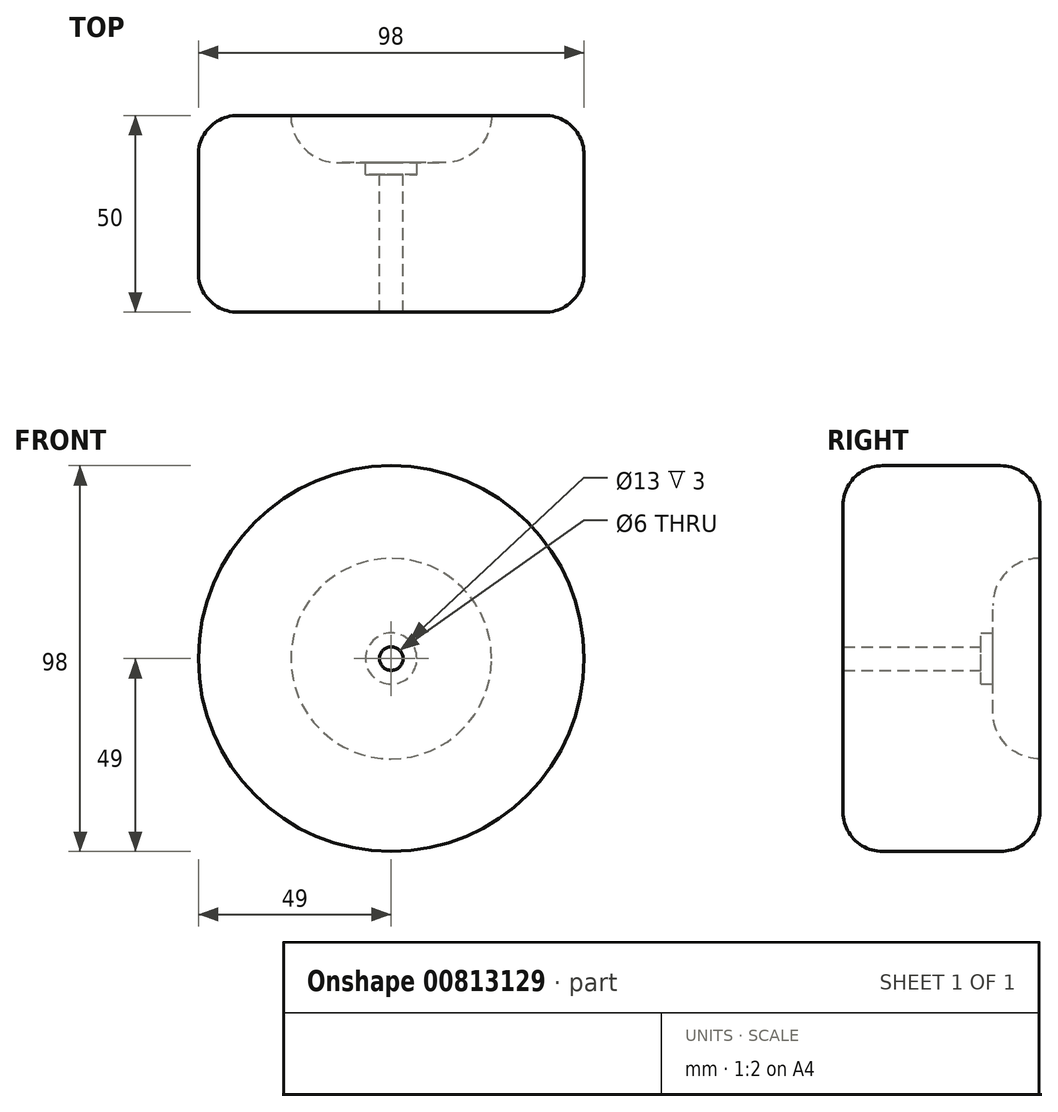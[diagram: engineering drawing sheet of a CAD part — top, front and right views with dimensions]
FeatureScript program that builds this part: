
annotation { "Feature Type Name" : "Feature", "Feature Type Description" : "" }
export const myFeature = defineFeature(function(context is Context, id is Id, definition is map)
    precondition{}
    {
        {
            var Q0;
            Q0=qCreatedBy(makeId("Front.planeOp"),FACE);
            var sketch = newSketch(context, id + "F0", { "sketchPlane" : qUnion([Q0])});
            skCircle(sketch, "E0", {"center": v(0, 0) * mm, "radius": 49 * mm});
            skSolve(sketch);
        }
        {
            var Q0;
            Q0=qSketchRegion(id+"F0",true);
            extrude(context, id + "F1", {"entities" : qUnion([Q0]), "depth" : 50 * mm, "offsetDistance" : 25 * mm});
        }
        {
            var Q0;
            Q0=makeQuery(id+"F1.opExtrude","CAP_EDGE",EDGE,{"disambiguationData":[OSD([sQuery(id+"F0.wireOp",EDGE,"E0")])],"isStart":false});
            var Q1;
            Q1=makeQuery(id+"F1.opExtrude","CAP_EDGE",EDGE,{"disambiguationData":[OSD([sQuery(id+"F0.wireOp",EDGE,"E0")])],"isStart":true});
            fillet(context, id + "F2", {"entities" : qUnion([Q0, Q1]), "radius" : 10 * mm, "tangentPropagation" : true, "allowEdgeOverflow" : false});
        }
        {
            var Q0;
            Q0=qCreatedBy(makeId("Front.planeOp"),FACE);
            var sketch = newSketch(context, id + "F3", { "sketchPlane" : qUnion([Q0])});
            skArc(sketch, "E1", {"start": v(-4.5, 48.8) * mm, "mid": v(0, 47.5) * mm, "end": v(4.5, 48.8) * mm});
            skArc(sketch, "E2.0", {"start": v(-4.5, 48.8) * mm, "mid": v(-9.56, 48.06) * mm, "end": v(-14.5, 46.8) * mm});
            skArc(sketch, "E3.1.0", {"start": v(-22.83, 43.35) * mm, "mid": v(-18.18, 43.9) * mm, "end": v(-14.5, 46.8) * mm});
            skArc(sketch, "E3.2.0", {"start": v(-37.69, 31.32) * mm, "mid": v(-33.6, 33.6) * mm, "end": v(-31.32, 37.69) * mm});
            skArc(sketch, "E3.3.0", {"start": v(-46.8, 14.5) * mm, "mid": v(-43.9, 18.18) * mm, "end": v(-43.35, 22.83) * mm});
            skArc(sketch, "E3.4.0", {"start": v(-48.8, -4.5) * mm, "mid": v(-47.5, 0) * mm, "end": v(-48.8, 4.5) * mm});
            skArc(sketch, "E3.5.0", {"start": v(-43.35, -22.83) * mm, "mid": v(-43.9, -18.18) * mm, "end": v(-46.8, -14.5) * mm});
            skArc(sketch, "E3.6.0", {"start": v(-31.32, -37.69) * mm, "mid": v(-33.6, -33.6) * mm, "end": v(-37.69, -31.32) * mm});
            skArc(sketch, "E3.7.0", {"start": v(-14.5, -46.8) * mm, "mid": v(-18.18, -43.9) * mm, "end": v(-22.83, -43.35) * mm});
            skArc(sketch, "E3.8.0", {"start": v(4.5, -48.8) * mm, "mid": v(0, -47.5) * mm, "end": v(-4.5, -48.8) * mm});
            skArc(sketch, "E3.9.0", {"start": v(22.83, -43.35) * mm, "mid": v(18.18, -43.9) * mm, "end": v(14.5, -46.8) * mm});
            skArc(sketch, "E3.10.0", {"start": v(37.69, -31.32) * mm, "mid": v(33.6, -33.6) * mm, "end": v(31.32, -37.69) * mm});
            skArc(sketch, "E3.11.0", {"start": v(46.8, -14.5) * mm, "mid": v(43.9, -18.18) * mm, "end": v(43.35, -22.83) * mm});
            skArc(sketch, "E3.12.0", {"start": v(48.8, 4.5) * mm, "mid": v(47.5, 0) * mm, "end": v(48.8, -4.5) * mm});
            skArc(sketch, "E3.13.0", {"start": v(43.35, 22.83) * mm, "mid": v(43.9, 18.18) * mm, "end": v(46.8, 14.5) * mm});
            skArc(sketch, "E3.14.0", {"start": v(31.32, 37.69) * mm, "mid": v(33.6, 33.6) * mm, "end": v(37.69, 31.32) * mm});
            skArc(sketch, "E3.15.0", {"start": v(14.5, 46.8) * mm, "mid": v(18.18, 43.9) * mm, "end": v(22.83, 43.35) * mm});
            skArc(sketch, "E4.trimOffspring", {"start": v(-22.83, 43.35) * mm, "mid": v(-27.22, 40.74) * mm, "end": v(-31.32, 37.69) * mm});
            skArc(sketch, "E5.trimOffspring", {"start": v(-37.69, 31.32) * mm, "mid": v(-40.74, 27.22) * mm, "end": v(-43.35, 22.83) * mm});
            skArc(sketch, "E6.trimOffspring", {"start": v(-46.8, 14.5) * mm, "mid": v(-48.06, 9.56) * mm, "end": v(-48.8, 4.5) * mm});
            skArc(sketch, "E7.trimOffspring", {"start": v(-48.8, -4.5) * mm, "mid": v(-48.06, -9.56) * mm, "end": v(-46.8, -14.5) * mm});
            skArc(sketch, "E8.trimOffspring", {"start": v(-43.35, -22.83) * mm, "mid": v(-40.74, -27.22) * mm, "end": v(-37.69, -31.32) * mm});
            skArc(sketch, "E9.trimOffspring", {"start": v(-31.32, -37.69) * mm, "mid": v(-27.22, -40.74) * mm, "end": v(-22.83, -43.35) * mm});
            skArc(sketch, "E10.trimOffspring", {"start": v(-14.5, -46.8) * mm, "mid": v(-9.56, -48.06) * mm, "end": v(-4.5, -48.8) * mm});
            skArc(sketch, "E11.trimOffspring", {"start": v(4.5, -48.8) * mm, "mid": v(9.56, -48.06) * mm, "end": v(14.5, -46.8) * mm});
            skArc(sketch, "E12.trimOffspring", {"start": v(22.83, -43.35) * mm, "mid": v(27.22, -40.74) * mm, "end": v(31.32, -37.69) * mm});
            skArc(sketch, "E13.trimOffspring", {"start": v(37.69, -31.32) * mm, "mid": v(40.74, -27.22) * mm, "end": v(43.35, -22.83) * mm});
            skArc(sketch, "E14.trimOffspring", {"start": v(46.8, -14.5) * mm, "mid": v(48.06, -9.56) * mm, "end": v(48.8, -4.5) * mm});
            skArc(sketch, "E15.trimOffspring", {"start": v(48.8, 4.5) * mm, "mid": v(48.06, 9.56) * mm, "end": v(46.8, 14.5) * mm});
            skArc(sketch, "E16.trimOffspring", {"start": v(43.35, 22.83) * mm, "mid": v(40.74, 27.22) * mm, "end": v(37.69, 31.32) * mm});
            skArc(sketch, "E17.trimOffspring", {"start": v(31.32, 37.69) * mm, "mid": v(27.22, 40.74) * mm, "end": v(22.83, 43.35) * mm});
            skArc(sketch, "E18.trimOffspring", {"start": v(14.5, 46.8) * mm, "mid": v(9.56, 48.06) * mm, "end": v(4.5, 48.8) * mm});
            skSolve(sketch);
        }
        {
            var Q0;
            Q0=qCreatedBy(makeId("Front.planeOp"),FACE);
            var sketch = newSketch(context, id + "F4", { "sketchPlane" : qUnion([Q0])});
            skCircle(sketch, "E19", {"center": v(0, 0) * mm, "radius": 25.5 * mm});
            skCircle(sketch, "E20", {"center": v(0, 0) * mm, "radius": 6.5 * mm});
            skCircle(sketch, "E21", {"center": v(0, 0) * mm, "radius": 3 * mm});
            skSolve(sketch);
        }
        {
            var Q0;
            Q0=makeQuery(id+"F4.imprint","IMPRINT",FACE,{"disambiguationData":[TD([[makeQuery(id+"F4.imprint","IMPRINT",EDGE,{"derivedFrom":sQuery(id+"F4.wireOp",EDGE,"E19")}),1.0]])]});
            extrude(context, id + "F5", {"entities" : qUnion([Q0]), "operationType" : NewBodyOperationType.REMOVE, "depth" : 12 * mm, "offsetDistance" : 25 * mm});
        }
        {
            var Q0;
            Q0=makeQuery(id+"F5.boolean.opBoolean","SPLIT",FACE,{"disambiguationData":[TD([makeQuery(id+"F5.opExtrude","SWEPT_FACE",FACE,{"disambiguationData":[OSD([sQuery(id+"F4.wireOp",EDGE,"E20")])]})])],"derivedFrom":makeQuery(id+"F1.opExtrude","CAP_FACE",FACE,{"disambiguationData":[OSD([sQuery(id+"F0.wireOp",EDGE,"E0")])],"isStart":true})});
            extrude(context, id + "F6", {"entities" : qUnion([Q0]), "operationType" : NewBodyOperationType.REMOVE, "oppositeDirection" : true, "depth" : 15 * mm, "offsetDistance" : 25 * mm});
        }
        {
            var Q0;
            Q0=makeQuery(id+"F5.boolean.opBoolean","COPY",EDGE,{"derivedFrom":makeQuery(id+"F5.opExtrude","CAP_EDGE",EDGE,{"disambiguationData":[OSD([sQuery(id+"F4.wireOp",EDGE,"E19")])],"isStart":false})});
            fillet(context, id + "F7", {"entities" : qUnion([Q0]), "radius" : 12 * mm, "tangentPropagation" : true, "allowEdgeOverflow" : false});
        }
        {
            var Q0;
            Q0=makeQuery(id+"F4.imprint","IMPRINT",FACE,{"disambiguationData":[TD([[makeQuery(id+"F4.imprint","IMPRINT",EDGE,{"derivedFrom":sQuery(id+"F4.wireOp",EDGE,"E21")}),1.0]])]});
            var Q1;
            Q1=sQuery(id+"F4.wireOp",EDGE,"E21");
            extrude(context, id + "F8", {"entities" : qUnion([Q0]), "operationType" : NewBodyOperationType.REMOVE, "surfaceEntities" : qUnion([Q1]), "endBound" : BoundingType.THROUGH_ALL, "depth" : 25 * mm, "offsetDistance" : 25 * mm});
        }
    });
